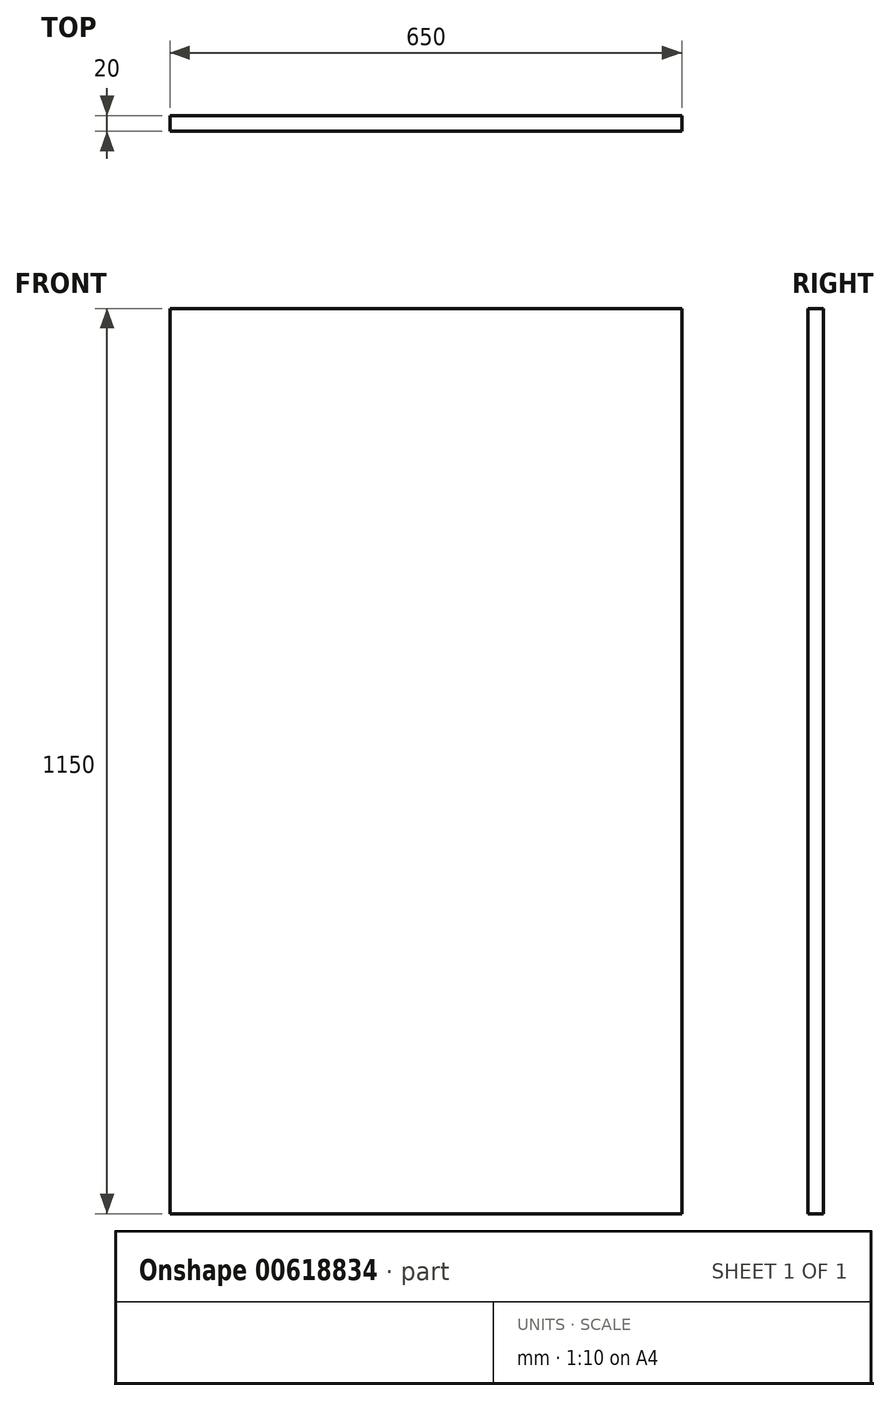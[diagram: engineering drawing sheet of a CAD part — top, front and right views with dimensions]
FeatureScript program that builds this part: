
annotation { "Feature Type Name" : "Feature", "Feature Type Description" : "" }
export const myFeature = defineFeature(function(context is Context, id is Id, definition is map)
    precondition{}
    {
        {
            var Q0;
            Q0=qCreatedBy(makeId("Front.planeOp"),FACE);
            var sketch = newSketch(context, id + "F0", { "sketchPlane" : qUnion([Q0])});
            skLineSegment(sketch, "E0.bottom", {"start": v(-325, 575) * mm, "end": v(325, 575) * mm});
            skLineSegment(sketch, "E0.top", {"start": v(-325, -575) * mm, "end": v(325, -575) * mm});
            skLineSegment(sketch, "E0.left", {"start": v(-325, 575) * mm, "end": v(-325, -575) * mm});
            skLineSegment(sketch, "E0.right", {"start": v(325, 575) * mm, "end": v(325, -575) * mm});
            skPoint(sketch, "E0.middle", {"position": v(0, 0) * mm});
            skSolve(sketch);
        }
        {
            var Q0;
            Q0 = qSketchRegion(id + "F0", true);
            extrude(context, id + "F1", {"entities" : qUnion([Q0]), "depth" : 20 * mm, "offsetDistance" : 25 * mm});
        }
    });
